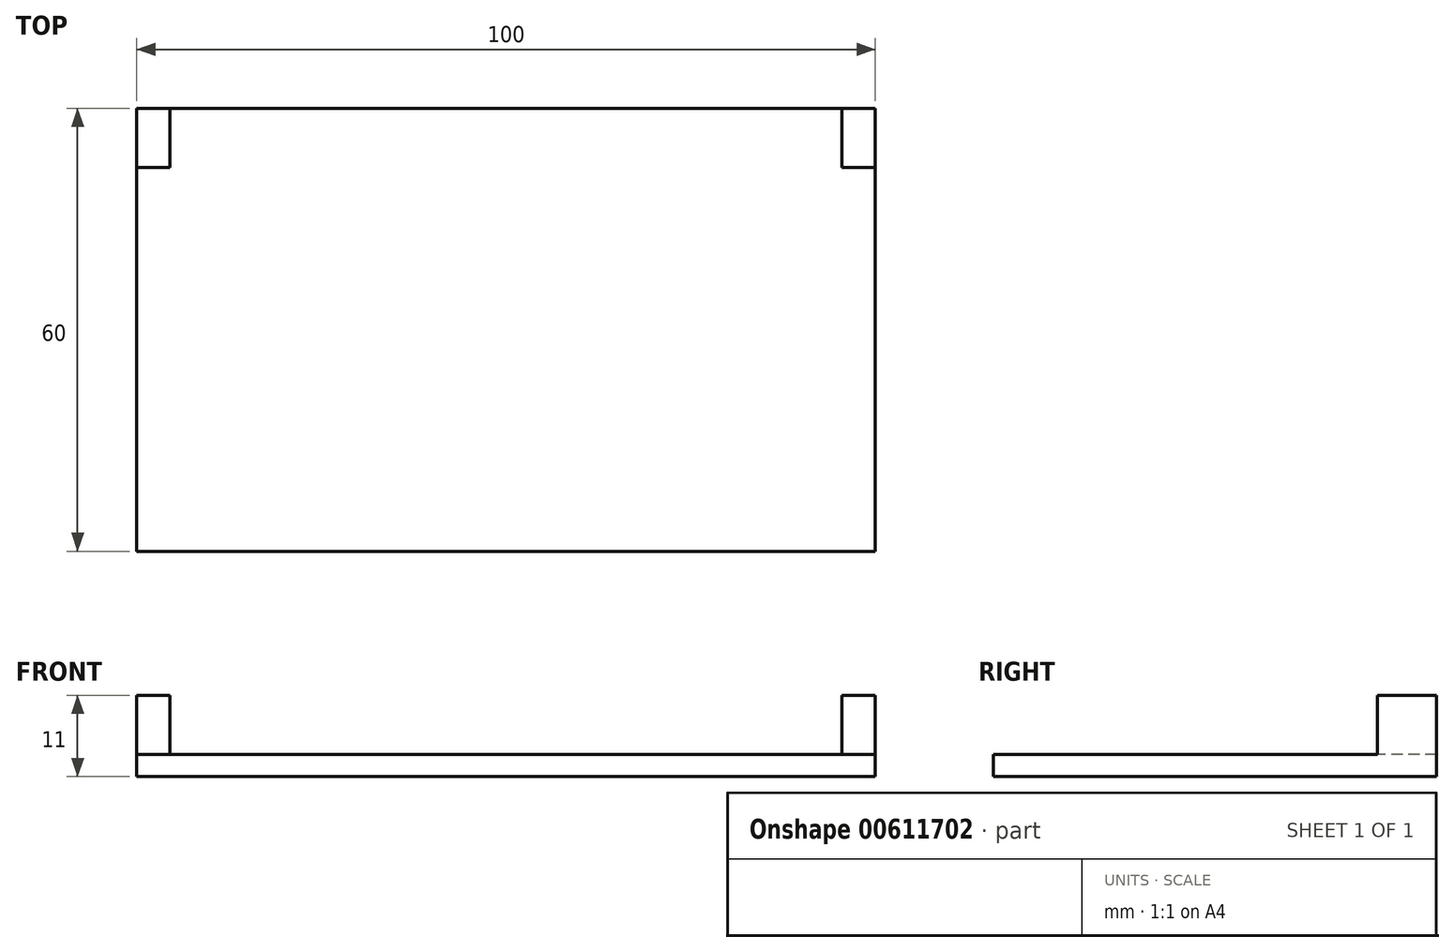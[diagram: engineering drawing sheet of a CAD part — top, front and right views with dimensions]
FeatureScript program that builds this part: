
annotation { "Feature Type Name" : "Feature", "Feature Type Description" : "" }
export const myFeature = defineFeature(function(context is Context, id is Id, definition is map)
    precondition{}
    {
        {
            var Q0;
            Q0=qCreatedBy(makeId("Top.planeOp"),FACE);
            var sketch = newSketch(context, id + "F0", { "sketchPlane" : qUnion([Q0])});
            skLineSegment(sketch, "E0.bottom", {"start": v(50, -30) * mm, "end": v(-50, -30) * mm});
            skLineSegment(sketch, "E0.top", {"start": v(50, 30) * mm, "end": v(-50, 30) * mm});
            skLineSegment(sketch, "E0.left", {"start": v(50, -30) * mm, "end": v(50, 30) * mm});
            skLineSegment(sketch, "E0.right", {"start": v(-50, -30) * mm, "end": v(-50, 30) * mm});
            skPoint(sketch, "E0.middle", {"position": v(0, 0) * mm});
            skPoint(sketch, "E1", {"position": v(50, 30) * mm});
            skPoint(sketch, "E2", {"position": v(-50, 30) * mm});
            skSolve(sketch);
        }
        {
            var Q0;
            Q0=makeQuery(id+"F0.imprint","IMPRINT",FACE,{"disambiguationData":[TD([[makeQuery(id+"F0.imprint","IMPRINT",EDGE,{"derivedFrom":sQuery(id+"F0.wireOp",EDGE,"E0.bottom")}),-1.0]])]});
            extrude(context, id + "F1", {"entities" : qUnion([Q0]), "depth" : 3 * mm, "offsetDistance" : 25 * mm});
        }
        {
            var Q0;
            Q0=makeQuery(id+"F1.opExtrude","CAP_FACE",FACE,{"disambiguationData":[OSD([sQuery(id+"F0.wireOp",EDGE,"E0.bottom"),sQuery(id+"F0.wireOp",EDGE,"E0.top"),sQuery(id+"F0.wireOp",EDGE,"E0.left"),sQuery(id+"F0.wireOp",EDGE,"E0.right")])],"isStart":false});
            var sketch = newSketch(context, id + "F2", { "sketchPlane" : qUnion([Q0])});
            skLineSegment(sketch, "E3.bottom", {"start": v(50, 30) * mm, "end": v(45.5, 30) * mm});
            skLineSegment(sketch, "E3.top", {"start": v(50, 22) * mm, "end": v(45.5, 22) * mm});
            skLineSegment(sketch, "E3.left", {"start": v(50, 30) * mm, "end": v(50, 22) * mm});
            skLineSegment(sketch, "E3.right", {"start": v(45.5, 30) * mm, "end": v(45.5, 22) * mm});
            skLineSegment(sketch, "E4.bottom", {"start": v(-50, 30) * mm, "end": v(-45.5, 30) * mm});
            skLineSegment(sketch, "E4.top", {"start": v(-50, 22) * mm, "end": v(-45.5, 22) * mm});
            skLineSegment(sketch, "E4.left", {"start": v(-50, 30) * mm, "end": v(-50, 22) * mm});
            skLineSegment(sketch, "E4.right", {"start": v(-45.5, 30) * mm, "end": v(-45.5, 22) * mm});
            skSolve(sketch);
        }
        {
            var Q0;
            Q0 = qSketchRegion(id + "F2", true);
            extrude(context, id + "F3", {"entities" : qUnion([Q0]), "operationType" : NewBodyOperationType.ADD, "depth" : 8 * mm, "offsetDistance" : 25 * mm});
        }
    });
